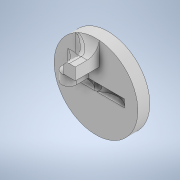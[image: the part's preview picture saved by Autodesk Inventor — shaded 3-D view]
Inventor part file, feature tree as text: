
AUTODESK INVENTOR PART (.ipt)
format: ipt  version: 2021 (Build 250183000, 183)  size: 259,584 bytes
history: native  units: mm
features: extrude x8, sketch x8, other x5, fillet x3, reference x1, projected_geometry x1
ambient origin geometry x8: Origin, YZ Plane, XZ Plane, XY Plane, X Axis, Y Axis, Z Axis, Center Point
bodies: Solid1 (feature_tree)
feature tree (26):
  extrude  "Extrusion1"  Depth=10.0mm TaperAngle=0.0deg
  extrude  "Extrusion2"  Depth=3.6mm TaperAngle=0.0deg
  extrude  "Extrusion3"  Depth=3.6mm TaperAngle=0.0deg
  extrude  "Extrusion4"  Depth=39.0mm
  fillet  "Fillet1"  Radius=2.7mm
  fillet  "Fillet2"  Radius=3.0mm
  extrude  "Extrusion5"  Depth=10.0mm
  extrude  "Extrusion6"  Depth=20.0mm TaperAngle=0.0deg
  extrude  "Extrusion7"  Depth=10.0mm
  fillet  "Fillet3"  Radius=20.0mm
  extrude  "Extrusion8"  Depth=10.0mm
  sketch  "Sketch1"  dims[d0=70.0mm d1=10.0mm d2=0.0mm]
  sketch  "Sketch2"  dims[d3=21.0mm d4=3.6mm d5=0.0mm]
  sketch  "Sketch3"  dims[d6=6.0mm d7=3.6mm d8=0.0mm]
  sketch  "Sketch4"  dims[d9=40.5mm d10=39.0mm d11=2.7mm d12=3.0mm]
  sketch  "Sketch5"  dims[d13=10.0mm d14=10.0mm]
  sketch  "Sketch6"  dims[d15=12.5mm d16=20.0mm d17=0.0mm]
  reference  "Reference1"
  sketch  "Sketch7"  dims[d18=10.0mm d19=5.0mm d20=20.0mm]
  projected_geometry  "Projected Loop1"
  sketch  "Sketch8"  dims[d21=8.0mm d22=3.0mm d23=20.0mm d24=0.0mm d25=3.6mm d26=10.0mm d27=0.0mm d28=12.0mm d29=10.0mm d30=0.0mm d31=5.0mm d32=30.5mm d33=20.0mm d35=25.0mm d36=10.0mm d38=10.0mm d40=3.0mm d41=3.4mm d42=0.0mm d43=0.0mm]
  parser-record x1  (decoder bookkeeping rows leaked as tree rows — omitted from the tree; the rows remain in map.json)
  other  "Złożenie gripper.iam"
  other  "przekładnia gripper:1"
  other  "Spur Gears:1"
  other  "Spur Gear2:1"
note: 1 file-system path scrubbed to <path> (originals preserved in map.json)
